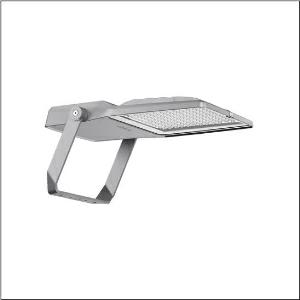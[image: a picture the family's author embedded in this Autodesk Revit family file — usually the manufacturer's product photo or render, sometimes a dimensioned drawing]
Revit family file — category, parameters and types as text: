
# Revit family: floodlight_fl_21_iq_midi___rs12_5xa7782f4b1a_76e1
name_source: partatom
category: Lighting Fixtures
units: mm (PartAtom-declared; Revit-internal decimal feet)

## family parameters
Cut with Voids When Loaded = No
Host = Face
Light Source = No
Part Type = Normal
Room Calculation Point = No
Round Connector Dimension = Use Diameter
Shared = No

## types (1)
- --- (1 x LED, 37160 lm, 270.2 W, 4000K)
    Apparent Load = 270 VA
    CIE Flux Codes = 79 92 99 100 100
    Color Rendering = 70
    Color Temperature = 4000K
    Default Elevation = 1800 mm
    Description = Floodlight FL 21 iQ midi, floodlight, primary light control with lens, of PMMA, primary optical cover: protective disc, of toughened safety glass, transparent, light distribution: RS12, light emission: direct distribution, installation type: surface-mounted, LED, High Power LED, rated luminous flux: 37.160lm, luminous efficacy: 138lm/W, light colour: 740, colour temperature: 4000K, control gear: ECG iQ, control: optimised constant luminous flux control (CLO 2.0), Desk-Remote (wireless, voltage-free reading and setting of iQ features in the workshop via application-optimized NFC function/RFID function), Smart-Wire, Night-Set, Temp-Guard, Street-Remote, Auto-Match, with terminal, 6-pole, mains connection: 220..240V, AC, 50/60Hz, start of lifetime: 270W, end of service life: 287W, reduction: 118W, luminaire housing, of diecast aluminium, powder-coated, Siteco® metallic grey (DB 702S), corrosivity category C5 mid according to DIN EN ISO 12944, sealing non-destructively replaceable, mounting bracket, of steel, galvanised, powder-coated, Siteco® metallic grey (DB 702S), protection rating (complete): IP66, insulation class (complete): insulation class II (safety insulation), certification: CE, protection symbol: D, impact resistance: IK08, permissible operating ambient temperature: -40..+40°C, permissible operating ambient temperature for outdoor applications: -40..+50°C, standard: DIN EN 12944, LABS conformity tested according to VDMA 24364:2018-05, packaging unit: 1 piece

Light Distribution: RS12
    Height = 76 mm
    Lamp = 1 x LED
    Lamp Light Flux = 37160 lm
    Lamp Power = 270.2 W
    Lamp count = 1
    Length = 657 mm
    Luminous efficacy = 138 lm/W
    Manufacturer = Siteco
    ModVariant = No
    Model = 5XA7782F4B1A
    Number of Poles = 1
    OnlyDefault = Yes
    Power Factor = 1
    Product Name = Floodlight FL 21 iQ midi | RS12
    Product group = floodlight | pylon annexe
    ProductGroupID = 6200
    Protection Class = Protection class II
    Protection Degree = IP 66
    RLX_Detail_Level = 1
    RLX_Emergency_Light_Flux = 0 lm
    RLX_Emergency_Type = 0
    RLX_Emergency_Type_DB = No
    RlxData = <blob elided: 141285 chars, md5=aa0c11e7>
    Socket = socket
    Standby Power = 0 W
    System Light Flux = 37160 lm
    System Power = 270 W
    Type Comments = factory setting: luminous flux: 100 % | dim-lin: 254 | 620 mA
    Type Image = l_1006876.jpg
    URL = http://relux.com
    VarID = @adj_037565
    Voltage = 0 V
    Weight = 0.00 kg
    Width = 442 mm

## geometry (parser evidence)
native form markers: Blend x4, Sweep x12
no freeform markers — native parametric forms only
